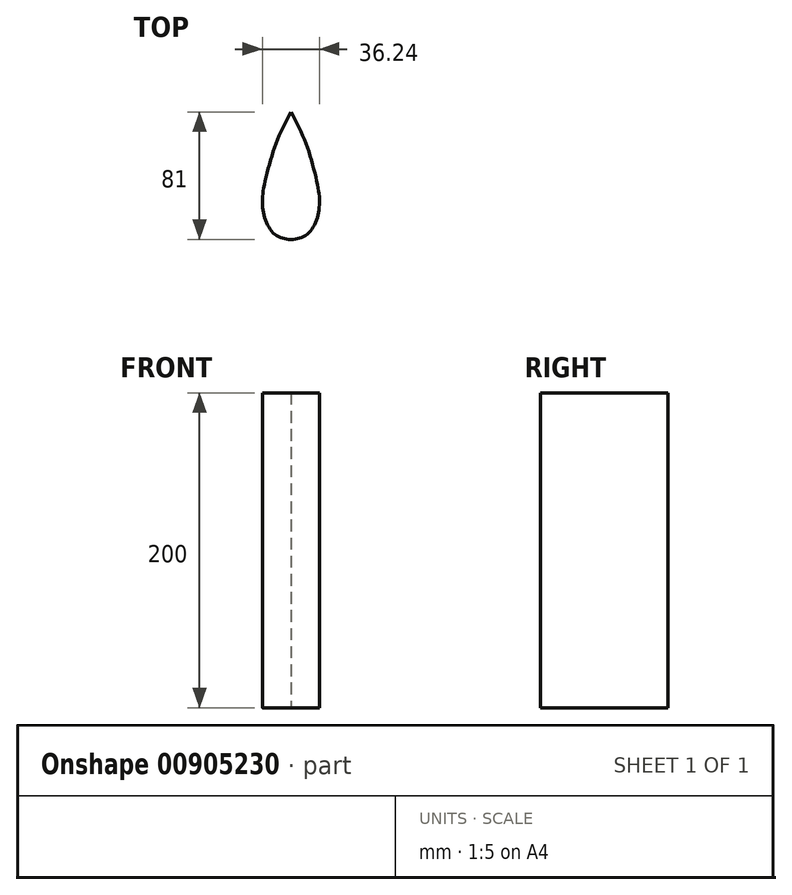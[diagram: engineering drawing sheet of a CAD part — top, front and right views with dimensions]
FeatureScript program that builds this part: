
annotation { "Feature Type Name" : "Feature", "Feature Type Description" : "" }
export const myFeature = defineFeature(function(context is Context, id is Id, definition is map)
    precondition{}
    {
        {
            var Q0;
            Q0=qCreatedBy(makeId("Top.planeOp"),FACE);
            var sketch = newSketch(context, id + "F0", { "sketchPlane" : qUnion([Q0])});
            skFitSpline(sketch, "E0", {"points": [v(0, 0) * mm, v(6.99, 1.23) * mm, v(12.73, 5.81) * mm, v(17.13, 15.06) * mm, v(18.12, 25.38) * mm], "startDerivative": vector(32.43, 0) * mm, "endDerivative": vector(0, 39.48) * mm});
            skLineSegment(sketch, "E1", {"start": v(18.12, 25.38) * mm, "end": v(18.12, 18.96) * mm});
            skFitSpline(sketch, "E2", {"points": [v(18.12, 25.38) * mm, v(17.18, 33.2) * mm, v(13.55, 48.3) * mm, v(7.97, 64.67) * mm, v(0, 81) * mm], "startDerivative": vector(0, 46.96) * mm, "endDerivative": vector(-30.24, 57.9) * mm});
            skLineSegment(sketch, "E3", {"start": v(0, 0) * mm, "end": v(0, 81) * mm});
            skFitSpline(sketch, "E4.MirrorCS", {"points": [v(-18.12, 25.38) * mm, v(-17.18, 33.2) * mm, v(-13.55, 48.3) * mm, v(-7.97, 64.67) * mm, v(0, 81) * mm], "startDerivative": vector(0, 46.96) * mm, "endDerivative": vector(30.24, 57.9) * mm});
            skFitSpline(sketch, "E5.MirrorCS", {"points": [v(0, 0) * mm, v(-6.99, 1.23) * mm, v(-12.73, 5.81) * mm, v(-17.13, 15.06) * mm, v(-18.12, 25.38) * mm], "startDerivative": vector(-32.43, 0) * mm, "endDerivative": vector(0, 39.48) * mm});
            skSolve(sketch);
        }
        {
            var Q0;
            Q0=makeQuery(id+"F0.imprint","IMPRINT",FACE,{"disambiguationData":[TD([[makeQuery(id+"F0.imprint","IMPRINT",EDGE,{"derivedFrom":sQuery(id+"F0.wireOp",EDGE,"E0")}),1.0]])]});
            var Q1;
            Q1=makeQuery(id+"F0.imprint","IMPRINT",FACE,{"disambiguationData":[TD([[makeQuery(id+"F0.imprint","IMPRINT",EDGE,{"derivedFrom":sQuery(id+"F0.wireOp",EDGE,"E3")}),1.0]])]});
            extrude(context, id + "F1", {"entities" : qUnion([Q0, Q1]), "depth" : 200 * mm, "offsetDistance" : 25 * mm});
        }
    });
